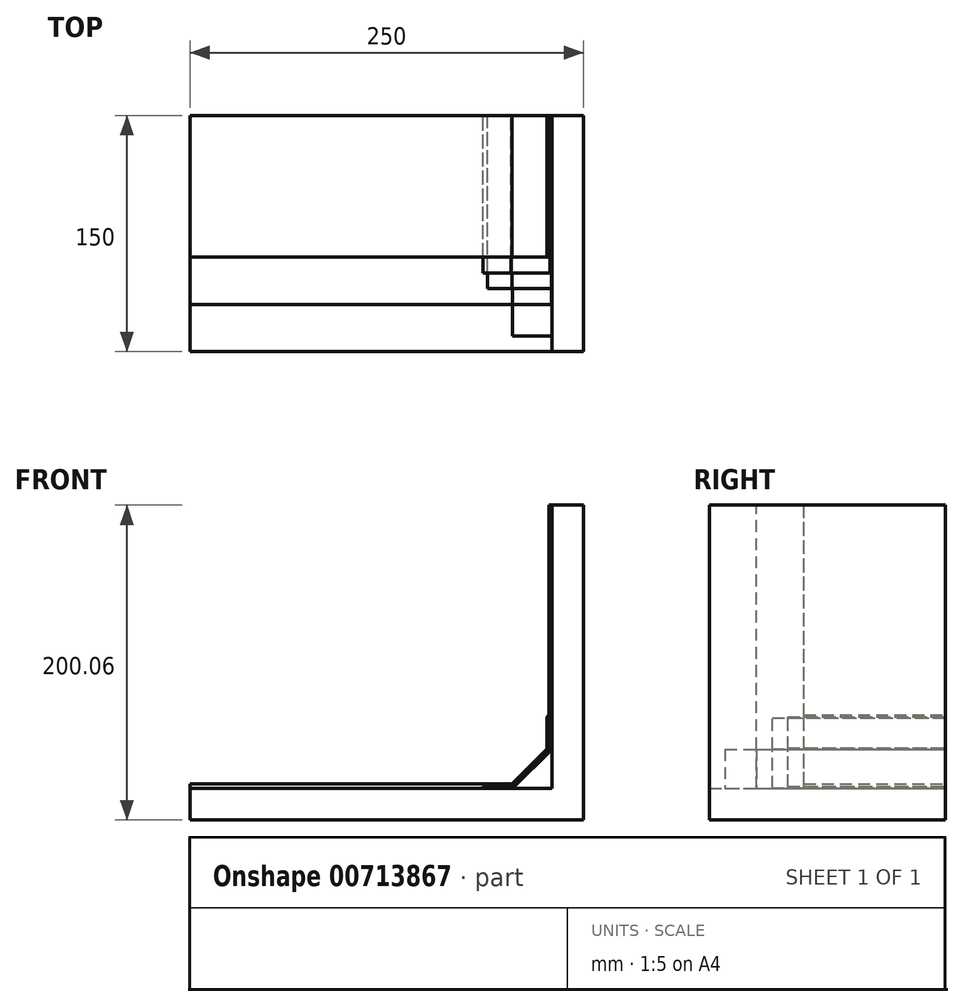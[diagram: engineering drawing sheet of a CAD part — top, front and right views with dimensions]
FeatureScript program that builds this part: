
annotation { "Feature Type Name" : "Feature", "Feature Type Description" : "" }
export const myFeature = defineFeature(function(context is Context, id is Id, definition is map)
    precondition{}
    {
        {
            var Q0;
            Q0=qCreatedBy(makeId("Front.planeOp"),FACE);
            var sketch = newSketch(context, id + "F0", { "sketchPlane" : qUnion([Q0])});
            skLineSegment(sketch, "E0", {"start": v(-201.96, -38.42) * mm, "end": v(28.04, -38.42) * mm});
            skLineSegment(sketch, "E1", {"start": v(28.04, -38.42) * mm, "end": v(28.04, 141.58) * mm});
            skLineSegment(sketch, "E2", {"start": v(28.04, 141.58) * mm, "end": v(48.04, 141.58) * mm});
            skLineSegment(sketch, "E3", {"start": v(48.04, 141.58) * mm, "end": v(48.04, -58.42) * mm});
            skLineSegment(sketch, "E4", {"start": v(48.04, -58.42) * mm, "end": v(-201.96, -58.42) * mm});
            skLineSegment(sketch, "E5", {"start": v(-201.96, -58.42) * mm, "end": v(-201.96, -38.42) * mm});
            skLineSegment(sketch, "E6", {"start": v(28.04, -13.42) * mm, "end": v(3.04, -38.42) * mm});
            skLineSegment(sketch, "E7", {"start": v(-201.96, -38.42) * mm, "end": v(-201.96, -38.22) * mm});
            skLineSegment(sketch, "E8", {"start": v(-201.96, -38.22) * mm, "end": v(2.8, -38.22) * mm});
            skLineSegment(sketch, "E9", {"start": v(2.8, -38.22) * mm, "end": v(27.84, -13.42) * mm});
            skLineSegment(sketch, "E10", {"start": v(27.84, -13.42) * mm, "end": v(27.84, 141.58) * mm});
            skLineSegment(sketch, "E11", {"start": v(27.84, 141.58) * mm, "end": v(28.04, 141.58) * mm});
            skLineSegment(sketch, "E12", {"start": v(-15.82, -38.22) * mm, "end": v(-15.82, -37.01) * mm});
            skLineSegment(sketch, "E13", {"start": v(-15.82, -37.01) * mm, "end": v(2.07, -37.01) * mm});
            skLineSegment(sketch, "E14", {"start": v(2.07, -37.01) * mm, "end": v(26.64, -12.67) * mm});
            skLineSegment(sketch, "E15", {"start": v(26.64, -12.67) * mm, "end": v(26.64, 6.97) * mm});
            skLineSegment(sketch, "E16", {"start": v(26.64, 6.97) * mm, "end": v(27.84, 6.97) * mm});
            skLineSegment(sketch, "E17", {"start": v(-12.86, -38.22) * mm, "end": v(-12.86, -38.01) * mm});
            skLineSegment(sketch, "E18", {"start": v(-12.86, -38.01) * mm, "end": v(2.7, -38.01) * mm});
            skLineSegment(sketch, "E19", {"start": v(2.7, -38.01) * mm, "end": v(27.66, -13.28) * mm});
            skLineSegment(sketch, "E20", {"start": v(27.66, -13.28) * mm, "end": v(27.66, 6.4) * mm});
            skLineSegment(sketch, "E21", {"start": v(27.66, 6.4) * mm, "end": v(27.84, 6.4) * mm});
            skLineSegment(sketch, "E22", {"start": v(-201.96, -38.22) * mm, "end": v(-201.96, -35.43) * mm});
            skLineSegment(sketch, "E23", {"start": v(-201.96, -35.43) * mm, "end": v(-20.26, -35.43) * mm});
            skLineSegment(sketch, "E24", {"start": v(-20.26, -35.43) * mm, "end": v(-12.86, -35.38) * mm});
            skLineSegment(sketch, "E25", {"start": v(-12.86, -35.38) * mm, "end": v(2.6, -35.38) * mm});
            skLineSegment(sketch, "E26", {"start": v(2.6, -35.38) * mm, "end": v(24.92, -13.28) * mm});
            skLineSegment(sketch, "E27", {"start": v(24.92, -13.28) * mm, "end": v(24.92, 7.15) * mm});
            skLineSegment(sketch, "E28", {"start": v(24.92, 7.15) * mm, "end": v(26.04, 8.26) * mm});
            skLineSegment(sketch, "E29", {"start": v(26.04, 8.26) * mm, "end": v(26.04, 141.64) * mm});
            skLineSegment(sketch, "E30", {"start": v(26.04, 141.64) * mm, "end": v(28.04, 141.58) * mm});
            skSolve(sketch);
        }
        {
            var Q0;
            {var subQ0=sQuery(id+"F0.wireOp",EDGE,"E2");Q0=makeQuery(id+"F0.imprint","IMPRINT",FACE,{"disambiguationData":[TD([[makeQuery(id+"F0.imprint","IMPRINT",EDGE,{"derivedFrom":subQ0}),-1.0]])]});}
            extrude(context, id + "F1", {"entities" : qUnion([Q0]), "depth" : 150 * mm});
        }
        {
            var Q0;
            {var subQ3=sQuery(id+"F0.wireOp",EDGE,"E6");Q0=makeQuery(id+"F0.imprint","IMPRINT",FACE,{"disambiguationData":[TD([[makeQuery(id+"F0.imprint","IMPRINT",EDGE,{"derivedFrom":subQ3}),1.0]])]});}
            extrude(context, id + "F2", {"entities" : qUnion([Q0]), "depth" : 140 * mm});
        }
        {
            var Q0;
            {var subQ9=sQuery(id+"F0.wireOp",EDGE,"E6");Q0=makeQuery(id+"F0.imprint","IMPRINT",FACE,{"disambiguationData":[TD([[makeQuery(id+"F0.imprint","IMPRINT",EDGE,{"derivedFrom":subQ9}),-1.0]])]});}
            extrude(context, id + "F3", {"entities" : qUnion([Q0]), "depth" : 120 * mm});
        }
        {
            var Q0;
            {var subQ1=sQuery(id+"F0.wireOp",EDGE,"E9");Q0=makeQuery(id+"F0.imprint","IMPRINT",FACE,{"disambiguationData":[TD([[makeQuery(id+"F0.imprint","IMPRINT",EDGE,{"derivedFrom":subQ1}),1.0]])]});}
            extrude(context, id + "F4", {"entities" : qUnion([Q0]), "depth" : 110 * mm});
        }
        {
            var Q0;
            {var subQ2=sQuery(id+"F0.wireOp",EDGE,"E12");Q0=makeQuery(id+"F0.imprint","IMPRINT",FACE,{"disambiguationData":[TD([[makeQuery(id+"F0.imprint","IMPRINT",EDGE,{"derivedFrom":subQ2}),-1.0]])]});}
            extrude(context, id + "F5", {"entities" : qUnion([Q0]), "depth" : 100 * mm});
        }
        {
            var Q0;
            {var subQ4=sQuery(id+"F0.wireOp",EDGE,"E11");Q0=makeQuery(id+"F0.imprint","IMPRINT",FACE,{"disambiguationData":[TD([[makeQuery(id+"F0.imprint","IMPRINT",EDGE,{"derivedFrom":subQ4}),1.0]])]});}
            extrude(context, id + "F6", {"entities" : qUnion([Q0]), "depth" : 90 * mm});
        }
    });
